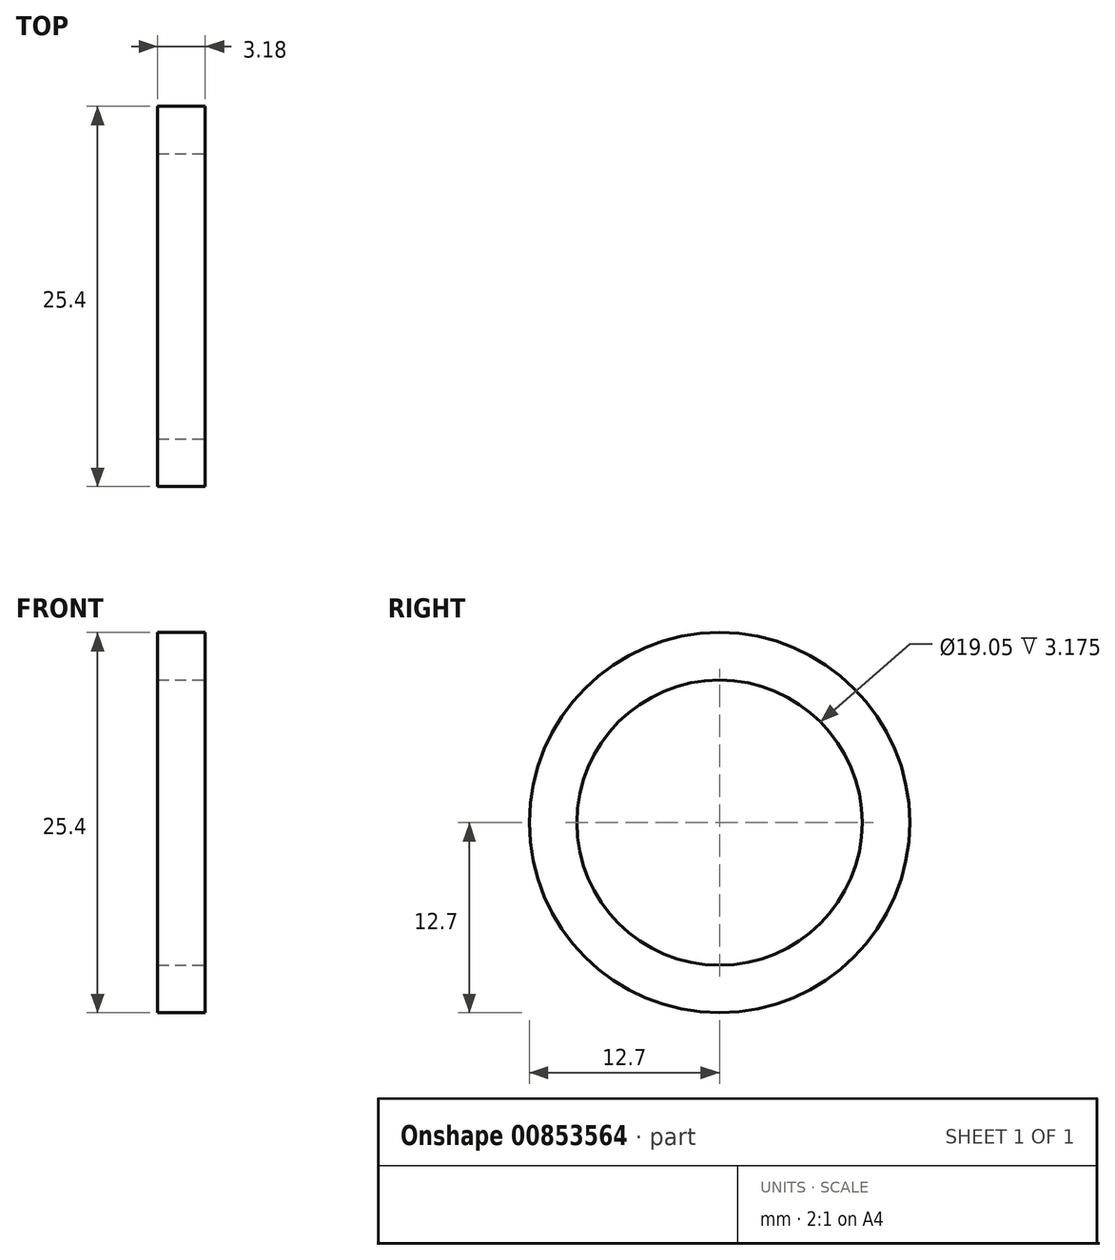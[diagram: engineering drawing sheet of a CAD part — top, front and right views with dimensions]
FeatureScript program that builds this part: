
annotation { "Feature Type Name" : "Feature", "Feature Type Description" : "" }
export const myFeature = defineFeature(function(context is Context, id is Id, definition is map)
    precondition{}
    {
        {
            var Q0;
            Q0=qCreatedBy(makeId("Right.planeOp"),FACE);
            var sketch = newSketch(context, id + "F0", { "sketchPlane" : qUnion([Q0])});
            skCircle(sketch, "E0", {"center": v(0, -0.72) * mm, "radius": 12.7 * mm});
            skCircle(sketch, "E1", {"center": v(0, -0.72) * mm, "radius": 9.53 * mm});
            skSolve(sketch);
        }
        {
            var Q0;
            Q0=qSketchRegion(id+"F0",true);
            extrude(context, id + "F1", {"entities" : qUnion([Q0]), "oppositeDirection" : true, "depth" : 3.17 * mm, "offsetDistance" : 25.4 * mm});
        }
    });
